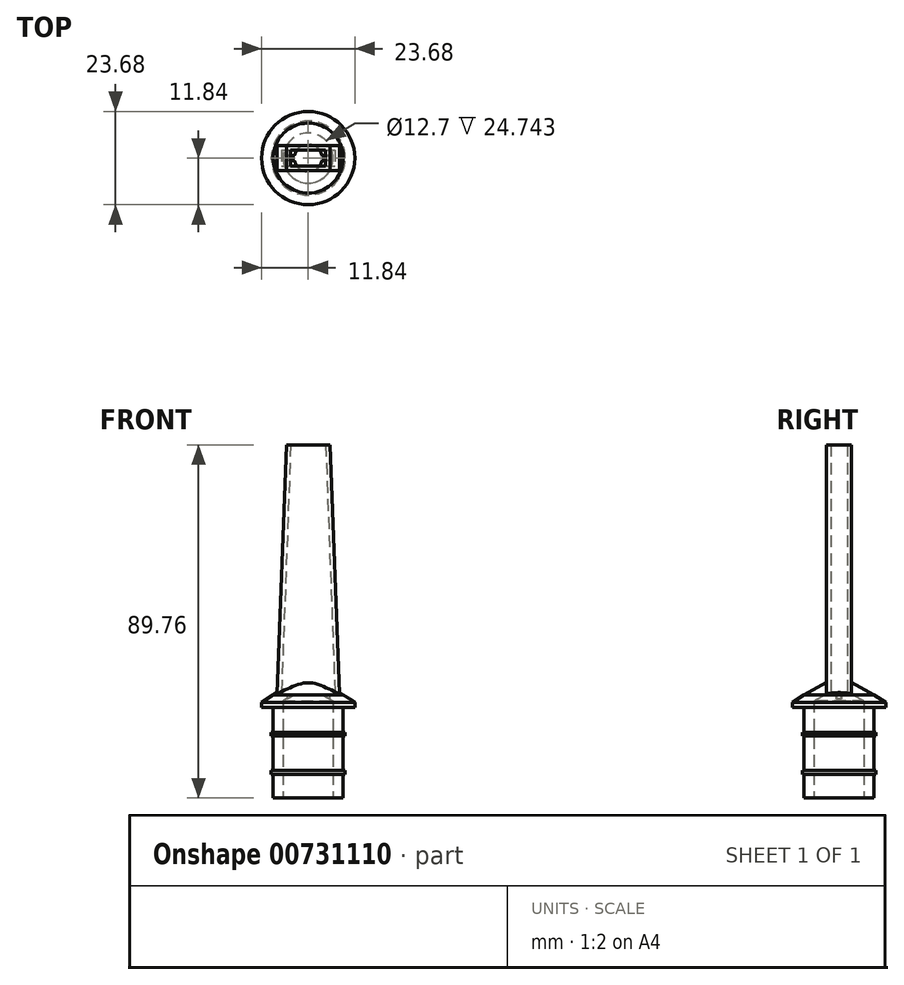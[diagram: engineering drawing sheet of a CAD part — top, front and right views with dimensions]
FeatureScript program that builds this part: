
annotation { "Feature Type Name" : "Feature", "Feature Type Description" : "" }
export const myFeature = defineFeature(function(context is Context, id is Id, definition is map)
    precondition{}
    {
        {
            var Q0;
            Q0=qCreatedBy(makeId("Top.planeOp"),FACE);
            var sketch = newSketch(context, id + "F0", { "sketchPlane" : qUnion([Q0])});
            skCircle(sketch, "E0", {"center": v(0, 0) * mm, "radius": 8.9 * mm});
            skSolve(sketch);
        }
        {
            var Q0;
            Q0 = qSketchRegion(id + "F0", true);
            extrude(context, id + "F1", {"entities" : qUnion([Q0]), "depth" : 6.05 * mm, "offsetDistance" : 25.4 * mm});
        }
        {
            var Q0;
            Q0=makeQuery(id+"F1.opExtrude","CAP_FACE",FACE,{"disambiguationData":[OSD([sQuery(id+"F0.wireOp",EDGE,"E0")])],"isStart":false});
            var sketch = newSketch(context, id + "F2", { "sketchPlane" : qUnion([Q0])});
            skCircle(sketch, "E1", {"center": v(0, 0) * mm, "radius": 9.39 * mm});
            skSolve(sketch);
        }
        {
            var Q0;
            Q0 = qSketchRegion(id + "F2", true);
            extrude(context, id + "F3", {"entities" : qUnion([Q0]), "operationType" : NewBodyOperationType.ADD, "depth" : 0.94 * mm, "offsetDistance" : 25.4 * mm});
        }
        {
            var Q0;
            Q0=makeQuery(id+"F3.opExtrude","CAP_FACE",FACE,{"disambiguationData":[OSD([sQuery(id+"F2.wireOp",EDGE,"E1")])],"isStart":false});
            var sketch = newSketch(context, id + "F4", { "sketchPlane" : qUnion([Q0])});
            skCircle(sketch, "E2", {"center": v(0, 0) * mm, "radius": 8.9 * mm});
            skSolve(sketch);
        }
        {
            var Q0;
            Q0=makeQuery(id+"F4.imprint","IMPRINT",FACE,{"disambiguationData":[TD([[makeQuery(id+"F4.imprint","IMPRINT",EDGE,{"derivedFrom":sQuery(id+"F4.wireOp",EDGE,"E2")}),1.0]])]});
            extrude(context, id + "F5", {"entities" : qUnion([Q0]), "operationType" : NewBodyOperationType.ADD, "depth" : 8.76 * mm, "offsetDistance" : 25.4 * mm});
        }
        {
            var Q0;
            Q0=makeQuery(id+"F5.opExtrude","CAP_FACE",FACE,{"disambiguationData":[OSD([sQuery(id+"F4.wireOp",EDGE,"E2")])],"isStart":false});
            var sketch = newSketch(context, id + "F6", { "sketchPlane" : qUnion([Q0])});
            skCircle(sketch, "E3", {"center": v(0, 0) * mm, "radius": 9.39 * mm});
            skSolve(sketch);
        }
        {
            var Q0;
            Q0 = qSketchRegion(id + "F6", true);
            extrude(context, id + "F7", {"entities" : qUnion([Q0]), "operationType" : NewBodyOperationType.ADD, "depth" : 1 * mm, "offsetDistance" : 25.4 * mm});
        }
        {
            var Q0;
            Q0=makeQuery(id+"F7.opExtrude","CAP_FACE",FACE,{"disambiguationData":[OSD([sQuery(id+"F6.wireOp",EDGE,"E3")])],"isStart":false});
            var sketch = newSketch(context, id + "F8", { "sketchPlane" : qUnion([Q0])});
            skCircle(sketch, "E4", {"center": v(0, 0) * mm, "radius": 8.9 * mm});
            skSolve(sketch);
        }
        {
            var Q0;
            Q0 = qSketchRegion(id + "F8", true);
            extrude(context, id + "F9", {"entities" : qUnion([Q0]), "operationType" : NewBodyOperationType.ADD, "depth" : 6.35 * mm, "offsetDistance" : 25.4 * mm});
        }
        {
            var Q0;
            Q0=qCreatedBy(makeId("Right.planeOp"),FACE);
            var sketch = newSketch(context, id + "F10", { "sketchPlane" : qUnion([Q0])});
            skLineSegment(sketch, "E5", {"start": v(0, 23.09) * mm, "end": v(-11.84, 23.09) * mm});
            skLineSegment(sketch, "E6", {"start": v(-11.84, 23.09) * mm, "end": v(-11.84, 24.36) * mm});
            skLineSegment(sketch, "E7", {"start": v(-11.84, 24.36) * mm, "end": v(-8.9, 26.26) * mm});
            skLineSegment(sketch, "E8", {"start": v(-8.9, 26.26) * mm, "end": v(0, 26.26) * mm});
            skLineSegment(sketch, "E9", {"start": v(0, 26.26) * mm, "end": v(0, 23.09) * mm});
            skSolve(sketch);
        }
        {
            var Q0;
            Q0=makeQuery(id+"F10.imprint","IMPRINT",FACE,{"disambiguationData":[TD([[makeQuery(id+"F10.imprint","IMPRINT",EDGE,{"derivedFrom":sQuery(id+"F10.wireOp",EDGE,"E5")}),-1.0]])]});
            var Q1;
            Q1=makeQuery(id+"F9.opExtrude","SWEPT_FACE",FACE,{"disambiguationData":[OSD([sQuery(id+"F8.wireOp",EDGE,"E4")])]});
            revolve(context, id + "F11", {"operationType" : NewBodyOperationType.ADD, "surfaceOperationType" : NewSurfaceOperationType.NEW, "entities" : qUnion([Q0]), "axis" : qUnion([Q1]), "revolveType" : RevolveType.FULL});
        }
        {
            var Q0;
            Q0=makeQuery(id+"F11.opRevolve","SWEPT_FACE",FACE,{"disambiguationData":[OSD([sQuery(id+"F10.wireOp",EDGE,"E8")])]});
            var sketch = newSketch(context, id + "F12", { "sketchPlane" : qUnion([Q0])});
            skCircle(sketch, "E10", {"center": v(0, 0) * mm, "radius": 8.9 * mm});
            skSolve(sketch);
        }
        {
            var Q0;
            Q0=makeQuery(id+"F12.imprint","IMPRINT",FACE,{"disambiguationData":[TD([[makeQuery(id+"F12.imprint","IMPRINT",EDGE,{"derivedFrom":sQuery(id+"F12.wireOp",EDGE,"E10")}),1.0]])]});
            cPlane(context, id + "F13", {"entities" : qUnion([Q0]), "cplaneType" : CPlaneType.OFFSET, "offset" : 0 * mm, "width" : 152.4 * mm, "height" : 152.4 * mm});
        }
        {
            var Q0;
            Q0=qCreatedBy(id+"F13.planeOp",FACE);
            var sketch = newSketch(context, id + "F14", { "sketchPlane" : qUnion([Q0])});
            skLineSegment(sketch, "E11.bottom", {"start": v(-7.94, 3.17) * mm, "end": v(7.94, 3.17) * mm});
            skLineSegment(sketch, "E11.top", {"start": v(-7.94, -3.18) * mm, "end": v(7.94, -3.18) * mm});
            skLineSegment(sketch, "E11.left", {"start": v(-7.94, 3.17) * mm, "end": v(-7.94, -3.18) * mm});
            skLineSegment(sketch, "E11.right", {"start": v(7.94, 3.17) * mm, "end": v(7.94, -3.18) * mm});
            skLineSegment(sketch, "E12", {"start": v(-7.94, 3.18) * mm, "end": v(7.94, -3.18) * mm, "construction": true});
            skPoint(sketch, "E13", {"position": v(0, 0) * mm});
            skSolve(sketch);
        }
        {
            var Q0;
            Q0=qCreatedBy(makeId("Right.planeOp"),FACE);
            var sketch = newSketch(context, id + "F15", { "sketchPlane" : qUnion([Q0])});
            skLineSegment(sketch, "E14", {"start": v(0, 26.26) * mm, "end": v(8.9, 26.26) * mm});
            skLineSegment(sketch, "E15", {"start": v(8.9, 26.26) * mm, "end": v(0, 31.03) * mm});
            skLineSegment(sketch, "E16", {"start": v(0, 31.03) * mm, "end": v(0, 26.26) * mm});
            skLineSegment(sketch, "E17", {"start": v(8.9, 26.26) * mm, "end": v(11.84, 24.36) * mm, "construction": true});
            skSolve(sketch);
        }
        {
            var Q0;
            Q0=makeQuery(id+"F15.imprint","IMPRINT",FACE,{"disambiguationData":[TD([[makeQuery(id+"F15.imprint","IMPRINT",EDGE,{"derivedFrom":sQuery(id+"F15.wireOp",EDGE,"E14")}),1.0]])]});
            var Q1;
            Q1=makeQuery(id+"F5.opExtrude","SWEPT_FACE",FACE,{"disambiguationData":[OSD([sQuery(id+"F4.wireOp",EDGE,"E2")])]});
            revolve(context, id + "F16", {"operationType" : NewBodyOperationType.ADD, "surfaceOperationType" : NewSurfaceOperationType.NEW, "entities" : qUnion([Q0]), "axis" : qUnion([Q1]), "revolveType" : RevolveType.FULL});
        }
        {
            var Q0;
            Q0=qCreatedBy(id+"F13.planeOp",FACE);
            cPlane(context, id + "F17", {"entities" : qUnion([Q0]), "cplaneType" : CPlaneType.OFFSET, "offset" : 63.5 * mm, "width" : 152.4 * mm, "height" : 152.4 * mm});
        }
        {
            var Q0;
            Q0=qCreatedBy(id+"F17.planeOp",FACE);
            var sketch = newSketch(context, id + "F18", { "sketchPlane" : qUnion([Q0])});
            skLineSegment(sketch, "E18.bottom", {"start": v(-5.56, 3.18) * mm, "end": v(5.56, 3.18) * mm});
            skLineSegment(sketch, "E18.top", {"start": v(-5.56, -3.18) * mm, "end": v(5.56, -3.18) * mm});
            skLineSegment(sketch, "E18.left", {"start": v(-5.56, 3.18) * mm, "end": v(-5.56, -3.18) * mm});
            skLineSegment(sketch, "E18.right", {"start": v(5.56, 3.18) * mm, "end": v(5.56, -3.18) * mm});
            skLineSegment(sketch, "E19", {"start": v(-5.56, 3.18) * mm, "end": v(5.56, -3.18) * mm, "construction": true});
            skPoint(sketch, "E20", {"position": v(0, 0) * mm});
            skSolve(sketch);
        }
        {
            var Q1;
            Q1 = qSketchRegion(id + "F14", true);
            var Q2;
            Q2 = qSketchRegion(id + "F18", true);
            loft(context, id + "F19", {"operationType" : NewBodyOperationType.ADD, "sheetProfilesArray" : [{ "sheetProfileEntities" : qUnion([Q1]) }, { "sheetProfileEntities" : qUnion([Q2]) }]});
        }
        {
            var Q0;
            Q0=makeQuery(id+"F19.opLoft","CAP_FACE",FACE,{"disambiguationData":[OSD([makeQuery(id+"F18.imprint","IMPRINT",FACE,{"disambiguationData":[TD([[makeQuery(id+"F18.imprint","IMPRINT",EDGE,{"derivedFrom":sQuery(id+"F18.wireOp",EDGE,"E18.bottom")}),-1.0]])]})])],"isStart":true});
            var sketch = newSketch(context, id + "F20", { "sketchPlane" : qUnion([Q0])});
            skLineSegment(sketch, "E21.bottom", {"start": v(-4.44, 2.06) * mm, "end": v(4.45, 2.06) * mm});
            skLineSegment(sketch, "E21.top", {"start": v(-4.44, -2.06) * mm, "end": v(4.45, -2.06) * mm});
            skLineSegment(sketch, "E21.left", {"start": v(-4.45, 2.06) * mm, "end": v(-4.45, -2.06) * mm});
            skLineSegment(sketch, "E21.right", {"start": v(4.45, 2.06) * mm, "end": v(4.45, -2.06) * mm});
            skSolve(sketch);
        }
        {
            var Q0;
            Q0=qCreatedBy(id+"F13.planeOp",FACE);
            var sketch = newSketch(context, id + "F21", { "sketchPlane" : qUnion([Q0])});
            skLineSegment(sketch, "E22.bottom", {"start": v(-6.82, 2.06) * mm, "end": v(6.82, 2.06) * mm});
            skLineSegment(sketch, "E22.top", {"start": v(-6.82, -2.06) * mm, "end": v(6.82, -2.06) * mm});
            skLineSegment(sketch, "E22.left", {"start": v(-6.82, 2.06) * mm, "end": v(-6.82, -2.06) * mm});
            skLineSegment(sketch, "E22.right", {"start": v(6.82, 2.06) * mm, "end": v(6.82, -2.06) * mm});
            skFitSpline(sketch, "E23.0", {"points": [v(-7.93, -3.18) * mm, v(-7.92, -2.13) * mm, v(-7.92, -0.8) * mm, v(-7.92, 0.79) * mm, v(-7.92, 1.86) * mm, v(-7.93, 2.65) * mm, v(-7.93, 3.17) * mm], "construction": true});
            skFitSpline(sketch, "E24.0", {"points": [v(7.93, 3.18) * mm, v(7.92, 2.13) * mm, v(7.92, 0.8) * mm, v(7.92, -0.79) * mm, v(7.92, -1.86) * mm, v(7.93, -2.65) * mm, v(7.93, -3.18) * mm], "construction": true});
            skSolve(sketch);
        }
        {
            var Q0;
            Q0 = qSketchRegion(id + "F20", true);
            var Q1;
            Q1 = qSketchRegion(id + "F21", true);
            loft(context, id + "F22", {"operationType" : NewBodyOperationType.REMOVE, "sheetProfilesArray" : [{ "sheetProfileEntities" : qUnion([Q0]) }, { "sheetProfileEntities" : qUnion([Q1]) }]});
        }
        {
            var Q0;
            Q0=makeQuery(id+"F22.boolean.opBoolean","COPY",FACE,{"derivedFrom":makeQuery(id+"F22.opLoft","CAP_FACE",FACE,{"disambiguationData":[OSD([makeQuery(id+"F21.imprint","IMPRINT",FACE,{"disambiguationData":[TD([[makeQuery(id+"F21.imprint","IMPRINT",EDGE,{"derivedFrom":sQuery(id+"F21.wireOp",EDGE,"E22.bottom")}),-1.0]])]})])],"isStart":true})});
            var Q1;
            Q1=makeQuery(id+"F1.opExtrude","CAP_FACE",FACE,{"disambiguationData":[OSD([sQuery(id+"F0.wireOp",EDGE,"E0")])],"isStart":true});
            shell(context, id + "F23", {"entities" : qUnion([Q0, Q1]), "thickness" : 2.54 * mm});
        }
    });
